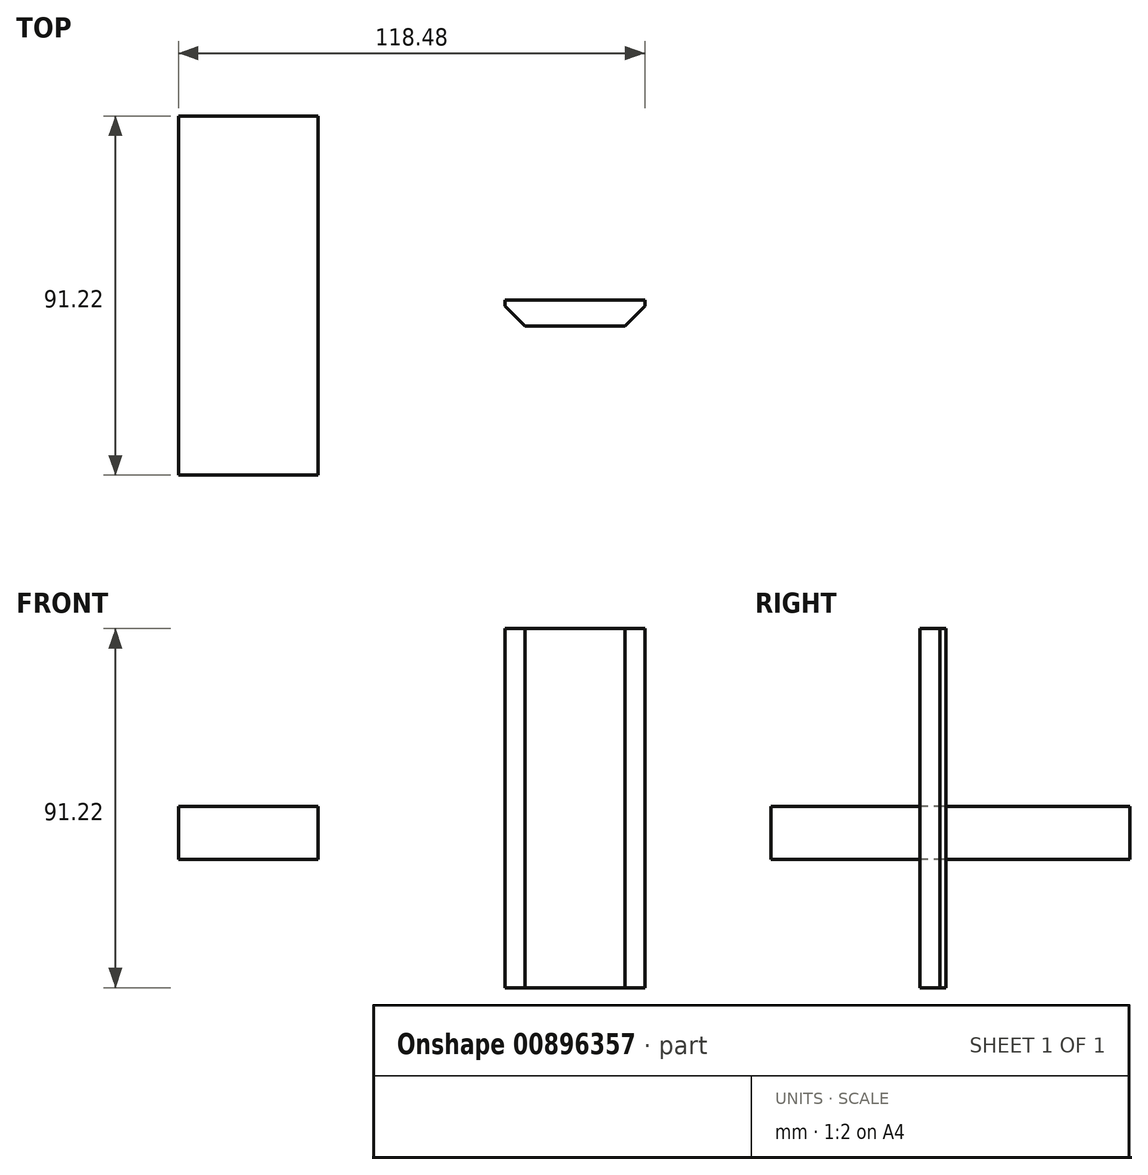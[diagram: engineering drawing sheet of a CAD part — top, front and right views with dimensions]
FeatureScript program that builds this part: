
annotation { "Feature Type Name" : "Feature", "Feature Type Description" : "" }
export const myFeature = defineFeature(function(context is Context, id is Id, definition is map)
    precondition{}
    {
        {
            var Q0;
            Q0=qCreatedBy(makeId("Top.planeOp"),FACE);
            var sketch = newSketch(context, id + "F0", { "sketchPlane" : qUnion([Q0])});
            skLineSegment(sketch, "E0.bottom", {"start": v(-53.32, 46.74) * mm, "end": v(-17.8, 46.74) * mm});
            skLineSegment(sketch, "E0.top", {"start": v(-53.32, -44.48) * mm, "end": v(-17.8, -44.48) * mm});
            skLineSegment(sketch, "E0.left", {"start": v(-53.32, 46.74) * mm, "end": v(-53.32, -44.48) * mm});
            skLineSegment(sketch, "E0.right", {"start": v(-17.8, 46.74) * mm, "end": v(-17.8, -44.48) * mm});
            skSolve(sketch);
        }
        {
            var Q0;
            Q0=makeQuery(id+"F0.imprint","IMPRINT",FACE,{"disambiguationData":[TD([[makeQuery(id+"F0.imprint","IMPRINT",EDGE,{"derivedFrom":sQuery(id+"F0.wireOp",EDGE,"E0.bottom")}),-1.0]])]});
            extrude(context, id + "F1", {"entities" : qUnion([Q0]), "depth" : 13.46 * mm, "offsetDistance" : 25.4 * mm});
        }
        {
            var Q0;
            Q0=qCreatedBy(makeId("Front.planeOp"),FACE);
            var sketch = newSketch(context, id + "F2", { "sketchPlane" : qUnion([Q0])});
            skLineSegment(sketch, "E1.bottom", {"start": v(29.64, 58.62) * mm, "end": v(65.16, 58.62) * mm});
            skLineSegment(sketch, "E1.top", {"start": v(29.64, -32.6) * mm, "end": v(65.16, -32.6) * mm});
            skLineSegment(sketch, "E1.left", {"start": v(29.64, 58.62) * mm, "end": v(29.64, -32.6) * mm});
            skLineSegment(sketch, "E1.right", {"start": v(65.16, 58.62) * mm, "end": v(65.16, -32.6) * mm});
            skSolve(sketch);
        }
        {
            var Q0;
            Q0=makeQuery(id+"F2.imprint","IMPRINT",FACE,{"disambiguationData":[TD([[makeQuery(id+"F2.imprint","IMPRINT",EDGE,{"derivedFrom":sQuery(id+"F2.wireOp",EDGE,"E1.bottom")}),-1.0]])]});
            var Q1;
            Q1 = qSketchRegion(id + "F2", true);
            extrude(context, id + "F3", {"entities" : qUnion([Q0, Q1]), "depth" : 6.6 * mm, "offsetDistance" : 25.4 * mm});
        }
        {
            var Q0;
            Q0=makeQuery(id+"F3.opExtrude","CAP_EDGE",EDGE,{"disambiguationData":[OSD([sQuery(id+"F2.wireOp",EDGE,"E1.right")])],"isStart":false});
            chamfer(context, id + "F4", {"entities" : qUnion([Q0]), "width" : 5.08 * mm, "tangentPropagation" : true});
        }
        {
            var Q0;
            Q0=makeQuery(id+"F3.opExtrude","CAP_EDGE",EDGE,{"disambiguationData":[OSD([sQuery(id+"F2.wireOp",EDGE,"E1.left")])],"isStart":false});
            chamfer(context, id + "F5", {"entities" : qUnion([Q0]), "width" : 5.08 * mm, "tangentPropagation" : true});
        }
    });
